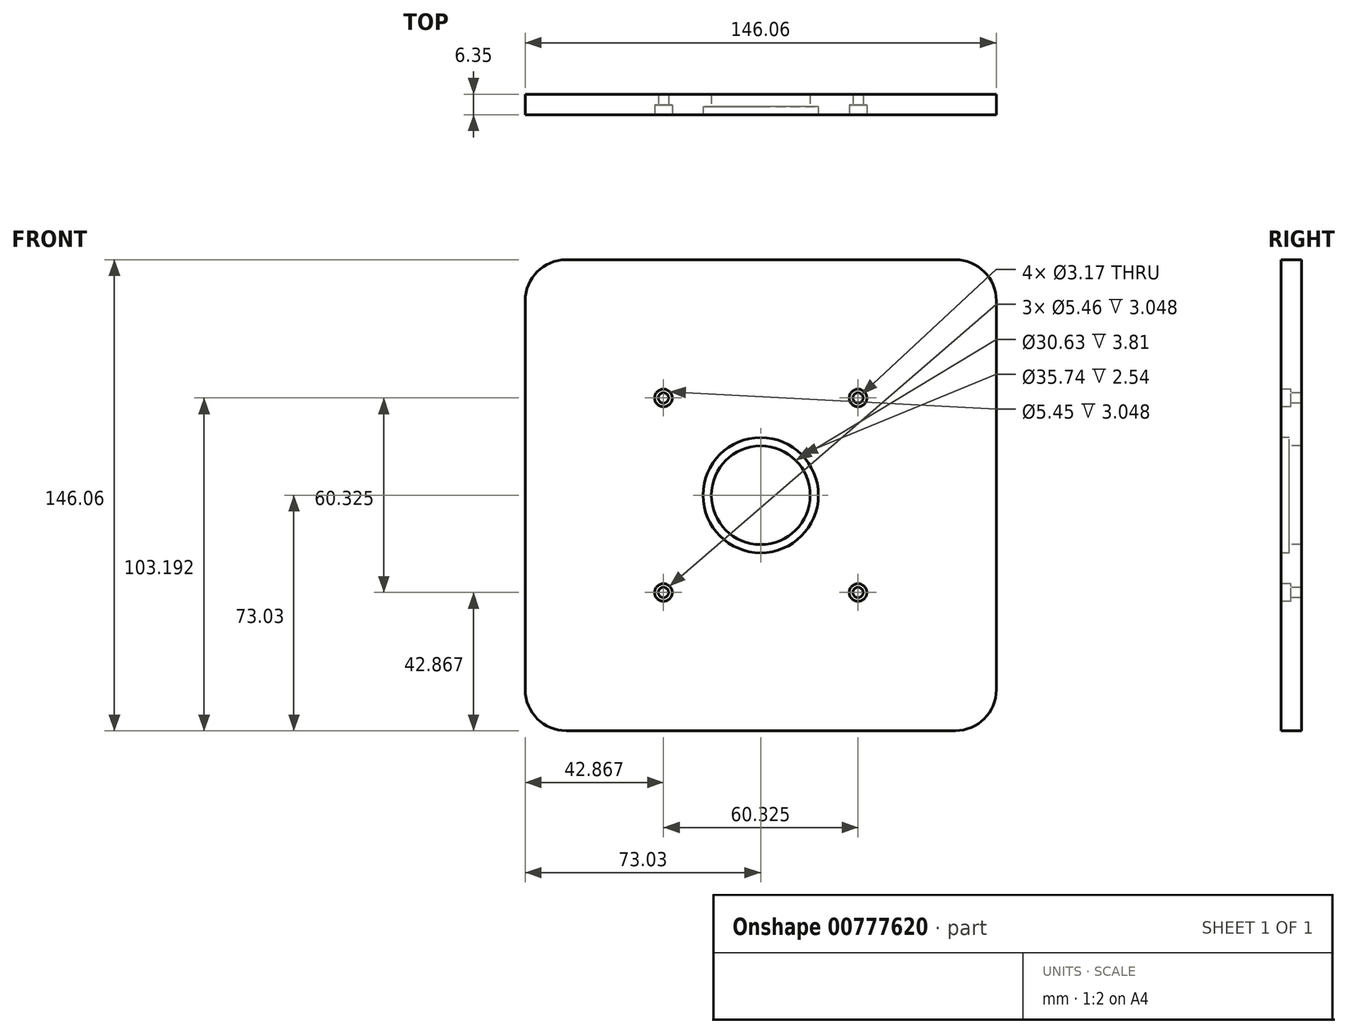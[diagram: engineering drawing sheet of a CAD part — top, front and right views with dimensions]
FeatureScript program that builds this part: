
annotation { "Feature Type Name" : "Feature", "Feature Type Description" : "" }
export const myFeature = defineFeature(function(context is Context, id is Id, definition is map)
    precondition{}
    {
        {
            var Q0;
            Q0=qCreatedBy(makeId("Front.planeOp"),FACE);
            var sketch = newSketch(context, id + "F0", { "sketchPlane" : qUnion([Q0])});
            skLineSegment(sketch, "E0.bottom", {"start": v(60.33, 73.02) * mm, "end": v(-60.32, 73.02) * mm});
            skLineSegment(sketch, "E0.top", {"start": v(60.33, -73.02) * mm, "end": v(-60.32, -73.02) * mm});
            skLineSegment(sketch, "E0.left", {"start": v(73.02, 60.33) * mm, "end": v(73.02, -60.32) * mm});
            skLineSegment(sketch, "E0.right", {"start": v(-73.02, 60.32) * mm, "end": v(-73.02, -60.32) * mm});
            skPoint(sketch, "E0.middle", {"position": v(0, 0) * mm});
            skPoint(sketch, "E1.visualSharp", {"position": v(73.02, 73.02) * mm});
            skArc(sketch, "E1.filletArc", {"start": v(73.03, 60.33) * mm, "mid": v(69.3, 69.3) * mm, "end": v(60.33, 73.03) * mm});
            skPoint(sketch, "E2.visualSharp", {"position": v(73.02, -73.02) * mm});
            skArc(sketch, "E2.filletArc", {"start": v(60.33, -73.02) * mm, "mid": v(69.3, -69.3) * mm, "end": v(73.03, -60.32) * mm});
            skPoint(sketch, "E3.visualSharp", {"position": v(-73.02, -73.02) * mm});
            skArc(sketch, "E3.filletArc", {"start": v(-73.02, -60.32) * mm, "mid": v(-69.3, -69.3) * mm, "end": v(-60.32, -73.02) * mm});
            skPoint(sketch, "E4.visualSharp", {"position": v(-73.02, 73.02) * mm});
            skArc(sketch, "E4.filletArc", {"start": v(-60.32, 73.02) * mm, "mid": v(-69.3, 69.3) * mm, "end": v(-73.02, 60.32) * mm});
            skSolve(sketch);
        }
        {
            var Q0;
            Q0=makeQuery(id+"F0.imprint","IMPRINT",FACE,{"disambiguationData":[TD([[makeQuery(id+"F0.imprint","IMPRINT",EDGE,{"derivedFrom":sQuery(id+"F0.wireOp",EDGE,"E0.bottom")}),1.0]])]});
            extrude(context, id + "F1", {"entities" : qUnion([Q0]), "depth" : 6.35 * mm, "offsetDistance" : 25.4 * mm});
        }
        {
            var Q0;
            Q0=makeQuery(id+"F1.opExtrude","CAP_FACE",FACE,{"disambiguationData":[OSD([sQuery(id+"F0.wireOp",EDGE,"E0.bottom"),sQuery(id+"F0.wireOp",EDGE,"E0.top"),sQuery(id+"F0.wireOp",EDGE,"E0.left"),sQuery(id+"F0.wireOp",EDGE,"E0.right"),sQuery(id+"F0.wireOp",EDGE,"E1.filletArc"),sQuery(id+"F0.wireOp",EDGE,"E2.filletArc"),sQuery(id+"F0.wireOp",EDGE,"E3.filletArc"),sQuery(id+"F0.wireOp",EDGE,"E4.filletArc")])],"isStart":false});
            var sketch = newSketch(context, id + "F2", { "sketchPlane" : qUnion([Q0])});
            skCircle(sketch, "E5", {"center": v(0, 0) * mm, "radius": 15.32 * mm});
            skCircle(sketch, "E6", {"center": v(0, 0) * mm, "radius": 17.87 * mm});
            skCircle(sketch, "E7", {"center": v(-30.16, 30.16) * mm, "radius": 1.59 * mm});
            skCircle(sketch, "E8", {"center": v(30.16, 30.16) * mm, "radius": 1.59 * mm});
            skCircle(sketch, "E9", {"center": v(30.16, -30.16) * mm, "radius": 1.59 * mm});
            skCircle(sketch, "E10", {"center": v(-30.16, -30.16) * mm, "radius": 1.59 * mm});
            skCircle(sketch, "E11", {"center": v(-30.16, 30.16) * mm, "radius": 2.73 * mm});
            skCircle(sketch, "E12", {"center": v(30.16, 30.16) * mm, "radius": 2.73 * mm});
            skCircle(sketch, "E13", {"center": v(30.16, -30.16) * mm, "radius": 2.73 * mm});
            skCircle(sketch, "E14", {"center": v(-30.16, -30.16) * mm, "radius": 2.73 * mm});
            skSolve(sketch);
        }
        {
            var Q0;
            Q0=makeQuery(id+"F2.imprint","IMPRINT",FACE,{"disambiguationData":[TD([[makeQuery(id+"F2.imprint","IMPRINT",EDGE,{"derivedFrom":sQuery(id+"F2.wireOp",EDGE,"E5")}),1.0]])]});
            extrude(context, id + "F3", {"entities" : qUnion([Q0]), "operationType" : NewBodyOperationType.REMOVE, "flatOperationType" : FlatOperationType.REMOVE, "oppositeDirection" : true, "depth" : 6.35 * mm, "offsetDistance" : 25.4 * mm, "domain" : OperationDomain.MODEL});
        }
        {
            var Q0;
            Q0=makeQuery(id+"F2.imprint","IMPRINT",FACE,{"disambiguationData":[TD([[makeQuery(id+"F2.imprint","IMPRINT",EDGE,{"derivedFrom":sQuery(id+"F2.wireOp",EDGE,"E5")}),-1.0]])]});
            extrude(context, id + "F4", {"entities" : qUnion([Q0]), "operationType" : NewBodyOperationType.REMOVE, "flatOperationType" : FlatOperationType.REMOVE, "oppositeDirection" : true, "depth" : 2.54 * mm, "offsetDistance" : 25.4 * mm, "domain" : OperationDomain.MODEL});
        }
        {
            var Q0;
            Q0=makeQuery(id+"F2.imprint","IMPRINT",FACE,{"disambiguationData":[TD([[makeQuery(id+"F2.imprint","IMPRINT",EDGE,{"derivedFrom":sQuery(id+"F2.wireOp",EDGE,"E8")}),1.0]])]});
            var Q1;
            Q1=makeQuery(id+"F2.imprint","IMPRINT",FACE,{"disambiguationData":[TD([[makeQuery(id+"F2.imprint","IMPRINT",EDGE,{"derivedFrom":sQuery(id+"F2.wireOp",EDGE,"E9")}),1.0]])]});
            var Q2;
            Q2=makeQuery(id+"F2.imprint","IMPRINT",FACE,{"disambiguationData":[TD([[makeQuery(id+"F2.imprint","IMPRINT",EDGE,{"derivedFrom":sQuery(id+"F2.wireOp",EDGE,"E7")}),1.0]])]});
            var Q3;
            Q3=makeQuery(id+"F2.imprint","IMPRINT",FACE,{"disambiguationData":[TD([[makeQuery(id+"F2.imprint","IMPRINT",EDGE,{"derivedFrom":sQuery(id+"F2.wireOp",EDGE,"E10")}),1.0]])]});
            extrude(context, id + "F5", {"entities" : qUnion([Q0, Q1, Q2, Q3]), "operationType" : NewBodyOperationType.REMOVE, "flatOperationType" : FlatOperationType.REMOVE, "oppositeDirection" : true, "depth" : 6.35 * mm, "offsetDistance" : 25.4 * mm, "domain" : OperationDomain.MODEL});
        }
        {
            var Q0;
            Q0=makeQuery(id+"F2.imprint","IMPRINT",FACE,{"disambiguationData":[TD([[makeQuery(id+"F2.imprint","IMPRINT",EDGE,{"derivedFrom":sQuery(id+"F2.wireOp",EDGE,"E10")}),-1.0]])]});
            var Q1;
            Q1=makeQuery(id+"F2.imprint","IMPRINT",FACE,{"disambiguationData":[TD([[makeQuery(id+"F2.imprint","IMPRINT",EDGE,{"derivedFrom":sQuery(id+"F2.wireOp",EDGE,"E9")}),-1.0]])]});
            var Q2;
            Q2=makeQuery(id+"F2.imprint","IMPRINT",FACE,{"disambiguationData":[TD([[makeQuery(id+"F2.imprint","IMPRINT",EDGE,{"derivedFrom":sQuery(id+"F2.wireOp",EDGE,"E8")}),-1.0]])]});
            var Q3;
            Q3=makeQuery(id+"F2.imprint","IMPRINT",FACE,{"disambiguationData":[TD([[makeQuery(id+"F2.imprint","IMPRINT",EDGE,{"derivedFrom":sQuery(id+"F2.wireOp",EDGE,"E7")}),-1.0]])]});
            extrude(context, id + "F6", {"entities" : qUnion([Q0, Q1, Q2, Q3]), "operationType" : NewBodyOperationType.REMOVE, "flatOperationType" : FlatOperationType.REMOVE, "oppositeDirection" : true, "depth" : 3.05 * mm, "offsetDistance" : 25.4 * mm, "domain" : OperationDomain.MODEL});
        }
    });
